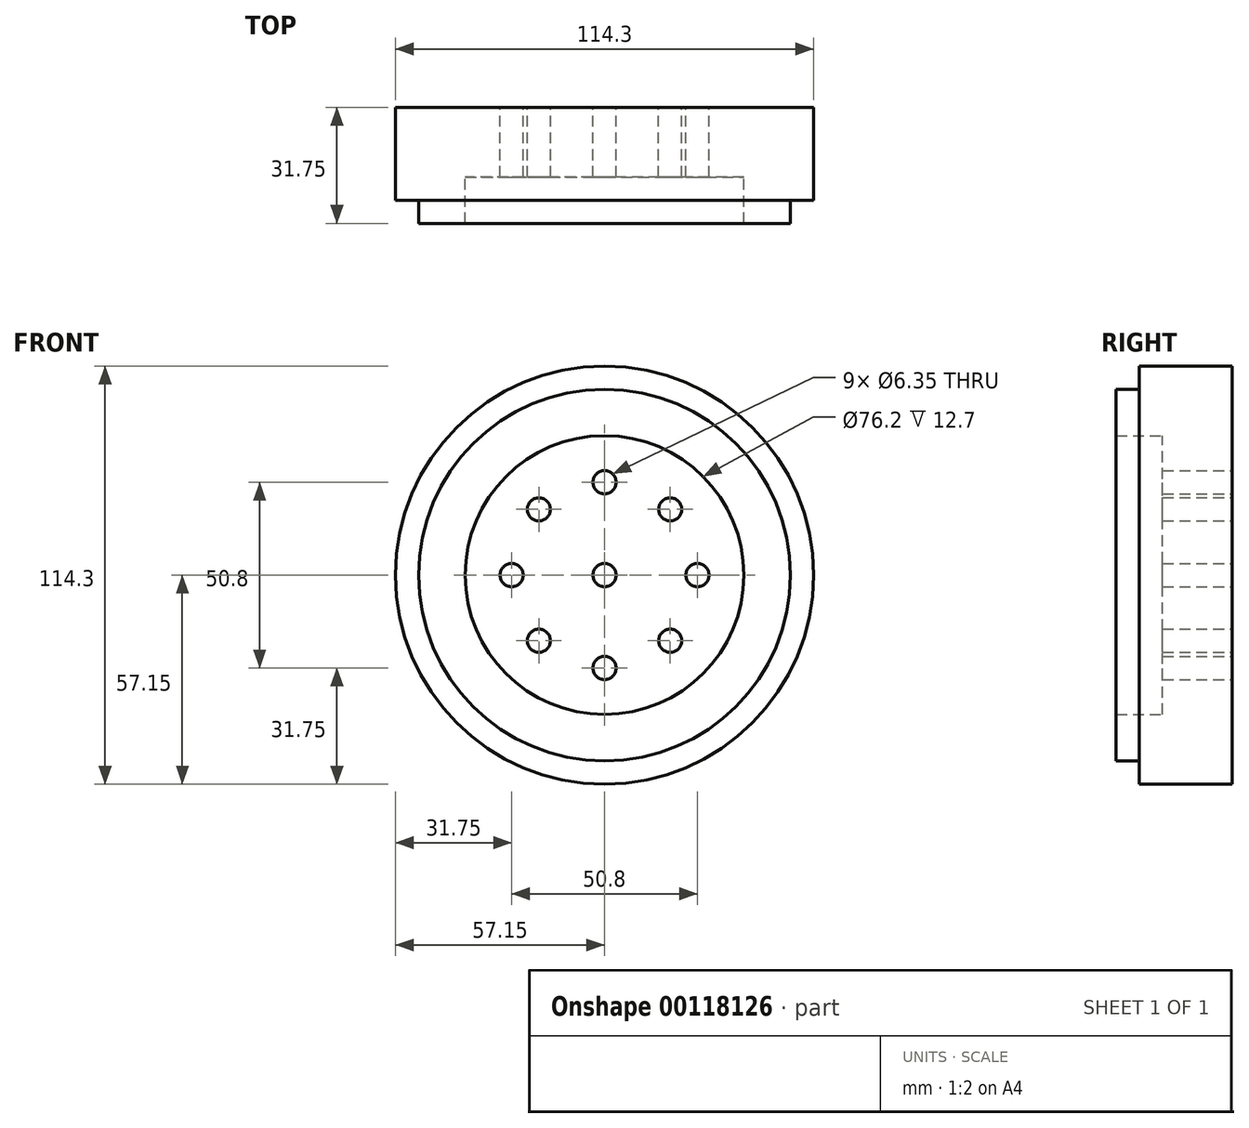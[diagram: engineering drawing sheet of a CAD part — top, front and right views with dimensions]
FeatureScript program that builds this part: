
annotation { "Feature Type Name" : "Feature", "Feature Type Description" : "" }
export const myFeature = defineFeature(function(context is Context, id is Id, definition is map)
    precondition{}
    {
        {
            var Q0;
            Q0=qCreatedBy(makeId("Front.planeOp"),FACE);
            var sketch = newSketch(context, id + "F0", { "sketchPlane" : qUnion([Q0])});
            skCircle(sketch, "E0", {"center": v(0, 0) * mm, "radius": 57.15 * mm});
            skCircle(sketch, "E1", {"center": v(0, 0) * mm, "radius": 50.8 * mm});
            skCircle(sketch, "E2", {"center": v(0, 0) * mm, "radius": 38.1 * mm});
            skCircle(sketch, "E3", {"center": v(0, 0) * mm, "radius": 25.4 * mm, "construction": true});
            skCircle(sketch, "E4", {"center": v(0, 25.4) * mm, "radius": 3.18 * mm});
            skCircle(sketch, "E5.1.0", {"center": v(-17.96, 17.96) * mm, "radius": 3.18 * mm});
            skCircle(sketch, "E5.2.0", {"center": v(-25.4, 0) * mm, "radius": 3.18 * mm});
            skCircle(sketch, "E5.3.0", {"center": v(-17.96, -17.96) * mm, "radius": 3.18 * mm});
            skCircle(sketch, "E5.4.0", {"center": v(0, -25.4) * mm, "radius": 3.18 * mm});
            skCircle(sketch, "E5.5.0", {"center": v(17.96, -17.96) * mm, "radius": 3.18 * mm});
            skCircle(sketch, "E5.6.0", {"center": v(25.4, 0) * mm, "radius": 3.18 * mm});
            skCircle(sketch, "E5.7.0", {"center": v(17.96, 17.96) * mm, "radius": 3.18 * mm});
            skCircle(sketch, "E6", {"center": v(0, 0) * mm, "radius": 3.18 * mm});
            skSolve(sketch);
        }
        {
            var Q0;
            Q0=makeQuery(id+"F0.imprint","IMPRINT",FACE,{"disambiguationData":[TD([[makeQuery(id+"F0.imprint","IMPRINT",EDGE,{"derivedFrom":sQuery(id+"F0.wireOp",EDGE,"E0")}),1.0]])]});
            extrude(context, id + "F1", {"entities" : qUnion([Q0]), "depth" : 25.4 * mm});
        }
        {
            var Q0;
            Q0=makeQuery(id+"F0.imprint","IMPRINT",FACE,{"disambiguationData":[TD([[makeQuery(id+"F0.imprint","IMPRINT",EDGE,{"derivedFrom":sQuery(id+"F0.wireOp",EDGE,"E1")}),1.0]])]});
            extrude(context, id + "F2", {"entities" : qUnion([Q0]), "operationType" : NewBodyOperationType.ADD, "depth" : 31.75 * mm});
        }
        {
            var Q0;
            Q0=makeQuery(id+"F0.imprint","IMPRINT",FACE,{"disambiguationData":[TD([[makeQuery(id+"F0.imprint","IMPRINT",EDGE,{"derivedFrom":sQuery(id+"F0.wireOp",EDGE,"E2")}),1.0]])]});
            extrude(context, id + "F3", {"entities" : qUnion([Q0]), "operationType" : NewBodyOperationType.ADD, "depth" : 19.05 * mm});
        }
    });
